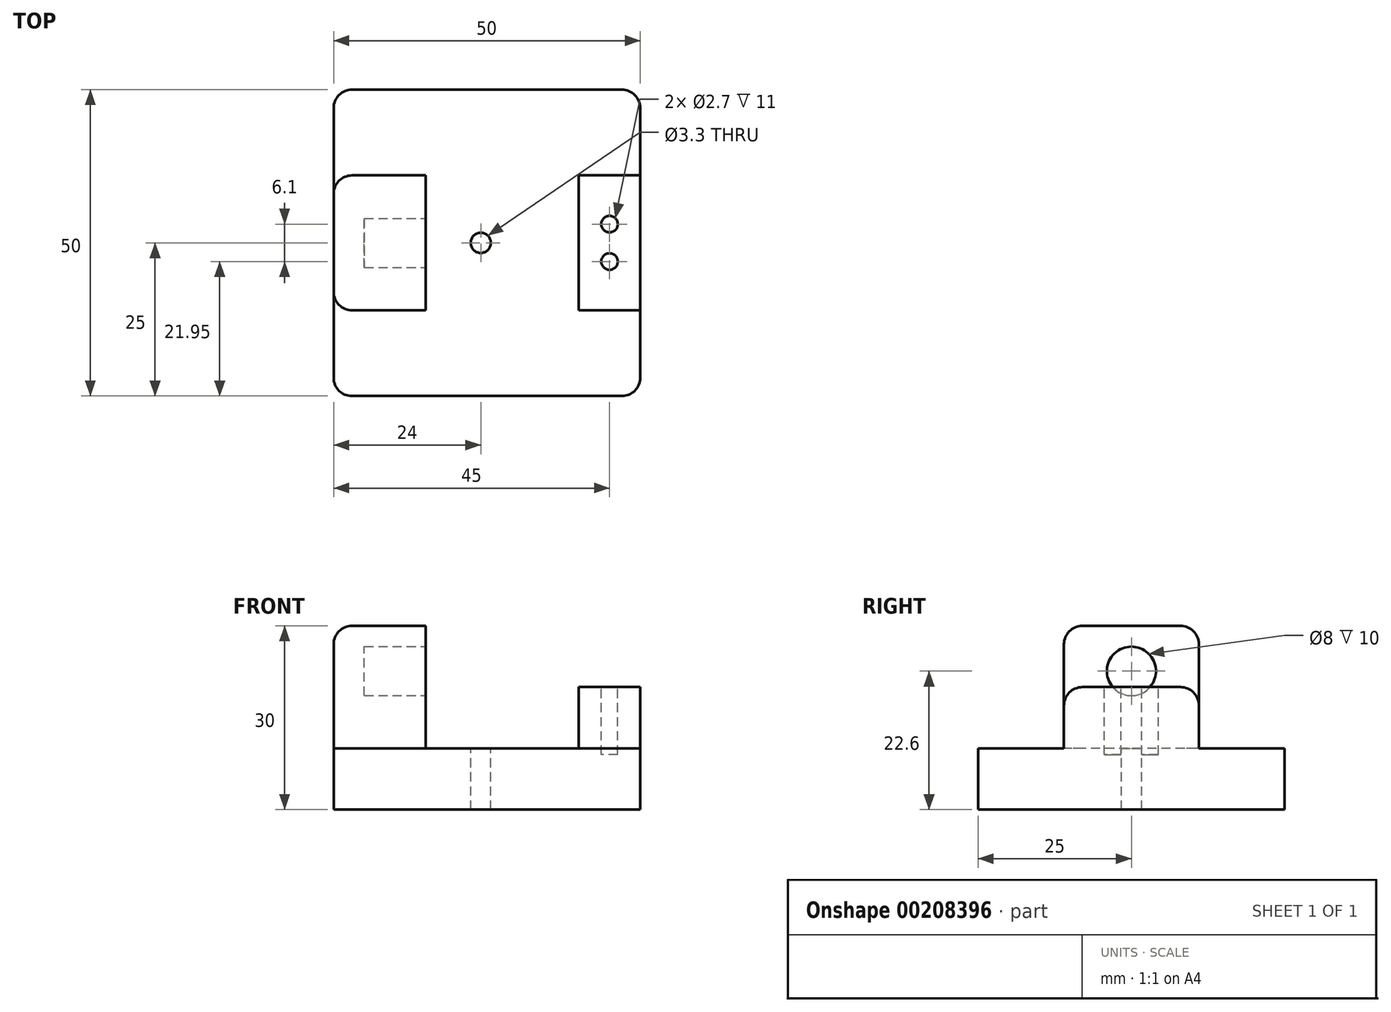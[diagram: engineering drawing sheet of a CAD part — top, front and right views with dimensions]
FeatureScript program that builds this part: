
annotation { "Feature Type Name" : "Feature", "Feature Type Description" : "" }
export const myFeature = defineFeature(function(context is Context, id is Id, definition is map)
    precondition{}
    {
        {
            var Q0;
            Q0=qCreatedBy(makeId("Top.planeOp"),FACE);
            var sketch = newSketch(context, id + "F0", { "sketchPlane" : qUnion([Q0])});
            skLineSegment(sketch, "E0.bottom", {"start": v(-15, 25) * mm, "end": v(35, 25) * mm});
            skLineSegment(sketch, "E0.top", {"start": v(-15, -25) * mm, "end": v(35, -25) * mm});
            skLineSegment(sketch, "E0.left", {"start": v(-15, 25) * mm, "end": v(-15, -25) * mm});
            skLineSegment(sketch, "E0.right", {"start": v(35, 25) * mm, "end": v(35, -25) * mm});
            skSolve(sketch);
        }
        {
            var Q0;
            Q0 = qSketchRegion(id + "F0", true);
            extrude(context, id + "F1", {"entities" : qUnion([Q0]), "depth" : 10 * mm});
        }
        {
            var Q0;
            Q0=makeQuery(id+"F1.opExtrude","CAP_FACE",FACE,{"disambiguationData":[OSD([sQuery(id+"F0.wireOp",EDGE,"E0.bottom"),sQuery(id+"F0.wireOp",EDGE,"E0.top"),sQuery(id+"F0.wireOp",EDGE,"E0.left"),sQuery(id+"F0.wireOp",EDGE,"E0.right")])],"isStart":false});
            var sketch = newSketch(context, id + "F2", { "sketchPlane" : qUnion([Q0])});
            skLineSegment(sketch, "E1.bottom", {"start": v(-15, 11) * mm, "end": v(0, 11) * mm});
            skLineSegment(sketch, "E1.top", {"start": v(-15, -11) * mm, "end": v(0, -11) * mm});
            skLineSegment(sketch, "E1.left", {"start": v(-15, 11) * mm, "end": v(-15, -11) * mm});
            skLineSegment(sketch, "E1.right", {"start": v(0, 11) * mm, "end": v(0, -11) * mm});
            skSolve(sketch);
        }
        {
            var Q0;
            Q0 = qSketchRegion(id + "F2", true);
            extrude(context, id + "F3", {"entities" : qUnion([Q0]), "operationType" : NewBodyOperationType.ADD, "depth" : 20 * mm});
        }
        {
            var Q0;
            Q0=makeQuery(id+"F3.opExtrude","SWEPT_FACE",FACE,{"disambiguationData":[OSD([sQuery(id+"F2.wireOp",EDGE,"E1.right")])]});
            var sketch = newSketch(context, id + "F4", { "sketchPlane" : qUnion([Q0])});
            skCircle(sketch, "E2", {"center": v(0, 22.6) * mm, "radius": 4 * mm});
            skSolve(sketch);
        }
        {
            var Q0;
            Q0 = qSketchRegion(id + "F4", true);
            extrude(context, id + "F5", {"entities" : qUnion([Q0]), "operationType" : NewBodyOperationType.REMOVE, "oppositeDirection" : true, "depth" : 10 * mm});
        }
        {
            var Q0;
            Q0=makeQuery(id+"F1.opExtrude","CAP_FACE",FACE,{"disambiguationData":[OSD([sQuery(id+"F0.wireOp",EDGE,"E0.bottom"),sQuery(id+"F0.wireOp",EDGE,"E0.top"),sQuery(id+"F0.wireOp",EDGE,"E0.left"),sQuery(id+"F0.wireOp",EDGE,"E0.right")])],"isStart":false});
            var sketch = newSketch(context, id + "F6", { "sketchPlane" : qUnion([Q0])});
            skLineSegment(sketch, "E3.bottom", {"start": v(0, 6.35) * mm, "end": v(13.5, 6.35) * mm, "construction": true});
            skLineSegment(sketch, "E3.top", {"start": v(0, -6.35) * mm, "end": v(13.5, -6.35) * mm, "construction": true});
            skLineSegment(sketch, "E3.left", {"start": v(0, 6.35) * mm, "end": v(0, -6.35) * mm, "construction": true});
            skLineSegment(sketch, "E3.right", {"start": v(13.5, 6.35) * mm, "end": v(13.5, -6.35) * mm, "construction": true});
            skCircle(sketch, "E4", {"center": v(9, 0) * mm, "radius": 1.65 * mm});
            skSolve(sketch);
        }
        {
            var Q0;
            Q0 = qSketchRegion(id + "F6", true);
            extrude(context, id + "F7", {"entities" : qUnion([Q0]), "operationType" : NewBodyOperationType.REMOVE, "endBound" : BoundingType.THROUGH_ALL, "oppositeDirection" : true, "depth" : 25 * mm});
        }
        {
            var Q0;
            Q0=makeQuery(id+"F1.opExtrude","CAP_FACE",FACE,{"disambiguationData":[OSD([sQuery(id+"F0.wireOp",EDGE,"E0.bottom"),sQuery(id+"F0.wireOp",EDGE,"E0.top"),sQuery(id+"F0.wireOp",EDGE,"E0.left"),sQuery(id+"F0.wireOp",EDGE,"E0.right")])],"isStart":false});
            var sketch = newSketch(context, id + "F8", { "sketchPlane" : qUnion([Q0])});
            skLineSegment(sketch, "E5.bottom", {"start": v(25, 11) * mm, "end": v(35, 11) * mm});
            skLineSegment(sketch, "E5.top", {"start": v(25, -11) * mm, "end": v(35, -11) * mm});
            skLineSegment(sketch, "E5.left", {"start": v(25, 11) * mm, "end": v(25, -11) * mm});
            skLineSegment(sketch, "E5.right", {"start": v(35, 11) * mm, "end": v(35, -11) * mm});
            skSolve(sketch);
        }
        {
            var Q0;
            Q0 = qSketchRegion(id + "F8", true);
            extrude(context, id + "F9", {"entities" : qUnion([Q0]), "operationType" : NewBodyOperationType.ADD, "depth" : 10 * mm});
        }
        {
            var Q0;
            Q0=makeQuery(id+"F9.opExtrude","CAP_FACE",FACE,{"disambiguationData":[OSD([sQuery(id+"F8.wireOp",EDGE,"E5.bottom"),sQuery(id+"F8.wireOp",EDGE,"E5.top"),sQuery(id+"F8.wireOp",EDGE,"E5.left"),sQuery(id+"F8.wireOp",EDGE,"E5.right")])],"isStart":false});
            var sketch = newSketch(context, id + "F10", { "sketchPlane" : qUnion([Q0])});
            skLineSegment(sketch, "E6", {"start": v(30, 13.95) * mm, "end": v(30, -15.96) * mm, "construction": true});
            skPoint(sketch, "E6.startSnap0", {"position": v(30, 11) * mm});
            skCircle(sketch, "E7", {"center": v(30, 3.05) * mm, "radius": 1.35 * mm});
            skCircle(sketch, "E8", {"center": v(30, -3.05) * mm, "radius": 1.35 * mm});
            skSolve(sketch);
        }
        {
            var Q0;
            Q0 = qSketchRegion(id + "F10", true);
            extrude(context, id + "F11", {"entities" : qUnion([Q0]), "operationType" : NewBodyOperationType.REMOVE, "oppositeDirection" : true, "depth" : 11 * mm});
        }
        {
            var Q0;
            Q0=makeQuery(id+"F3.opExtrude","CAP_EDGE",EDGE,{"disambiguationData":[OSD([sQuery(id+"F2.wireOp",EDGE,"E1.left")])],"isStart":false});
            var Q1;
            Q1=makeQuery(id+"F1.opExtrude","SWEPT_EDGE",EDGE,{"disambiguationData":[OSD([sQuery(id+"F0.wireOp",EDGE,"E0.top"),sQuery(id+"F0.wireOp",EDGE,"E0.left")])]});
            var Q2;
            Q2=makeQuery(id+"F1.opExtrude","SWEPT_EDGE",EDGE,{"disambiguationData":[OSD([sQuery(id+"F0.wireOp",EDGE,"E0.top"),sQuery(id+"F0.wireOp",EDGE,"E0.right")])]});
            var Q3;
            Q3=makeQuery(id+"F1.opExtrude","SWEPT_EDGE",EDGE,{"disambiguationData":[OSD([sQuery(id+"F0.wireOp",EDGE,"E0.bottom"),sQuery(id+"F0.wireOp",EDGE,"E0.right")])]});
            var Q4;
            Q4=makeQuery(id+"F1.opExtrude","SWEPT_EDGE",EDGE,{"disambiguationData":[OSD([sQuery(id+"F0.wireOp",EDGE,"E0.bottom"),sQuery(id+"F0.wireOp",EDGE,"E0.left")])]});
            var Q5;
            Q5=makeQuery(id+"F3.opExtrude","SWEPT_EDGE",EDGE,{"disambiguationData":[OSD([sQuery(id+"F0.wireOp",EDGE,"E0.left"),sQuery(id+"F2.wireOp",EDGE,"E1.bottom"),sQuery(id+"F2.wireOp",EDGE,"E1.left")])]});
            var Q6;
            Q6=makeQuery(id+"F3.opExtrude","SWEPT_EDGE",EDGE,{"disambiguationData":[OSD([sQuery(id+"F0.wireOp",EDGE,"E0.left"),sQuery(id+"F2.wireOp",EDGE,"E1.top"),sQuery(id+"F2.wireOp",EDGE,"E1.left")])]});
            var Q7;
            Q7=makeQuery(id+"F3.opExtrude","CAP_EDGE",EDGE,{"disambiguationData":[OSD([sQuery(id+"F2.wireOp",EDGE,"E1.bottom")])],"isStart":false});
            var Q8;
            Q8=makeQuery(id+"F3.opExtrude","CAP_EDGE",EDGE,{"disambiguationData":[OSD([sQuery(id+"F2.wireOp",EDGE,"E1.top")])],"isStart":false});
            var Q9;
            Q9=makeQuery(id+"F9.opExtrude","CAP_EDGE",EDGE,{"disambiguationData":[OSD([sQuery(id+"F8.wireOp",EDGE,"E5.bottom")])],"isStart":false});
            var Q10;
            Q10=makeQuery(id+"F9.opExtrude","CAP_EDGE",EDGE,{"disambiguationData":[OSD([sQuery(id+"F8.wireOp",EDGE,"E5.top")])],"isStart":false});
            fillet(context, id + "F12", {"entities" : qUnion([Q0, Q1, Q2, Q3, Q4, Q5, Q6, Q7, Q8, Q9, Q10]), "radius" : 3 * mm, "tangentPropagation" : true, "allowEdgeOverflow" : false});
        }
    });
